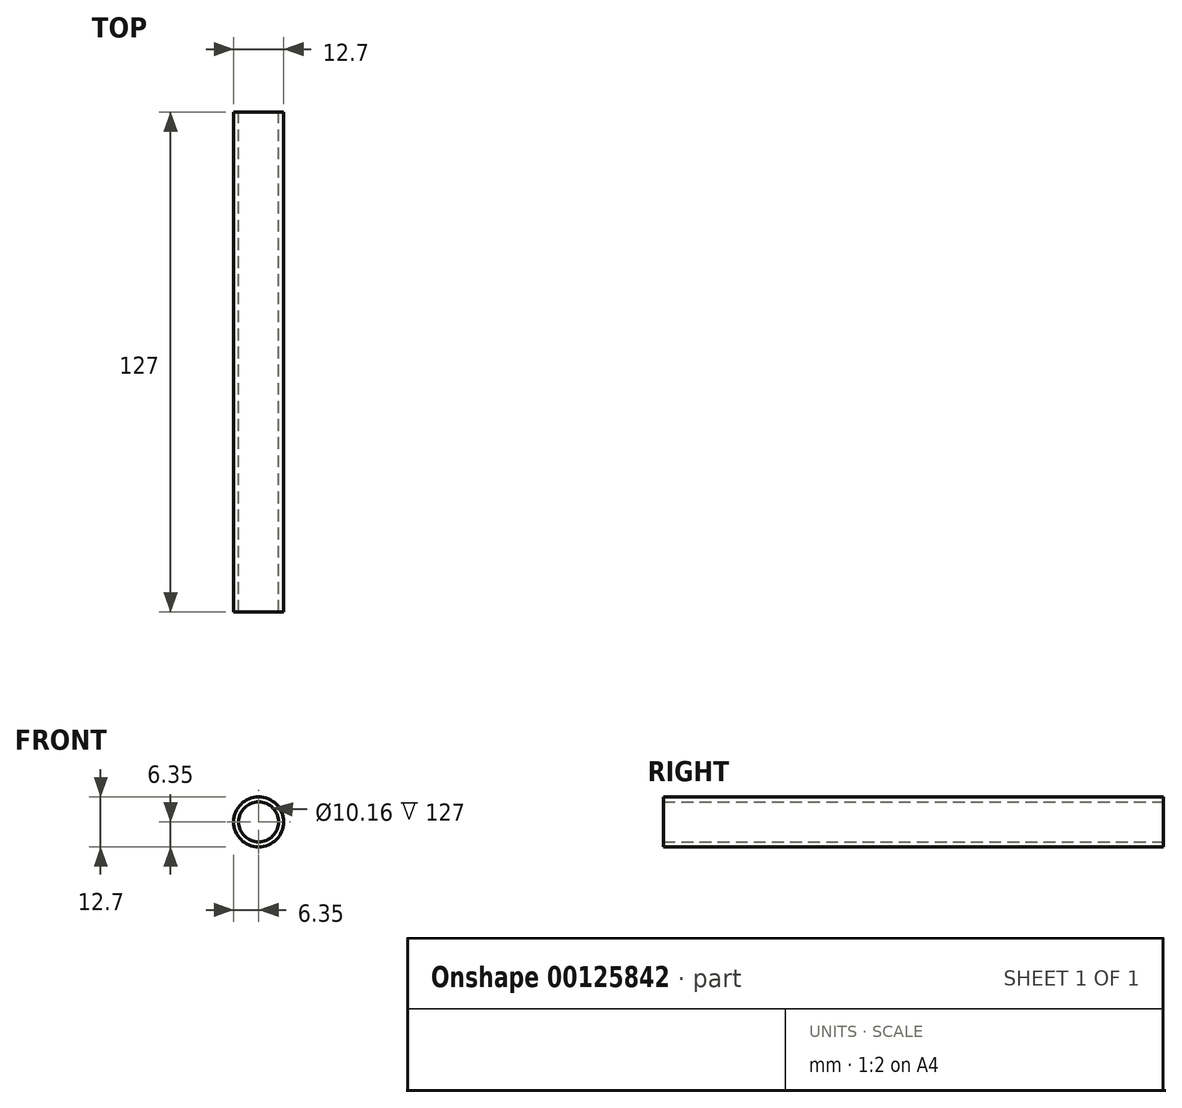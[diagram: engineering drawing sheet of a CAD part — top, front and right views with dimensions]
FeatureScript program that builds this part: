
annotation { "Feature Type Name" : "Feature", "Feature Type Description" : "" }
export const myFeature = defineFeature(function(context is Context, id is Id, definition is map)
    precondition{}
    {
        {
            var Q0;
            Q0=qCreatedBy(makeId("Front.planeOp"),FACE);
            var sketch = newSketch(context, id + "F0", { "sketchPlane" : qUnion([Q0])});
            skCircle(sketch, "E0", {"center": v(0, 0) * mm, "radius": 6.35 * mm});
            skCircle(sketch, "E1", {"center": v(0, 0) * mm, "radius": 5.08 * mm});
            skSolve(sketch);
        }
        {
            var Q0;
            Q0 = qSketchRegion(id + "F0", true);
            extrude(context, id + "F1", {"entities" : qUnion([Q0]), "depth" : 127 * mm});
        }
    });
